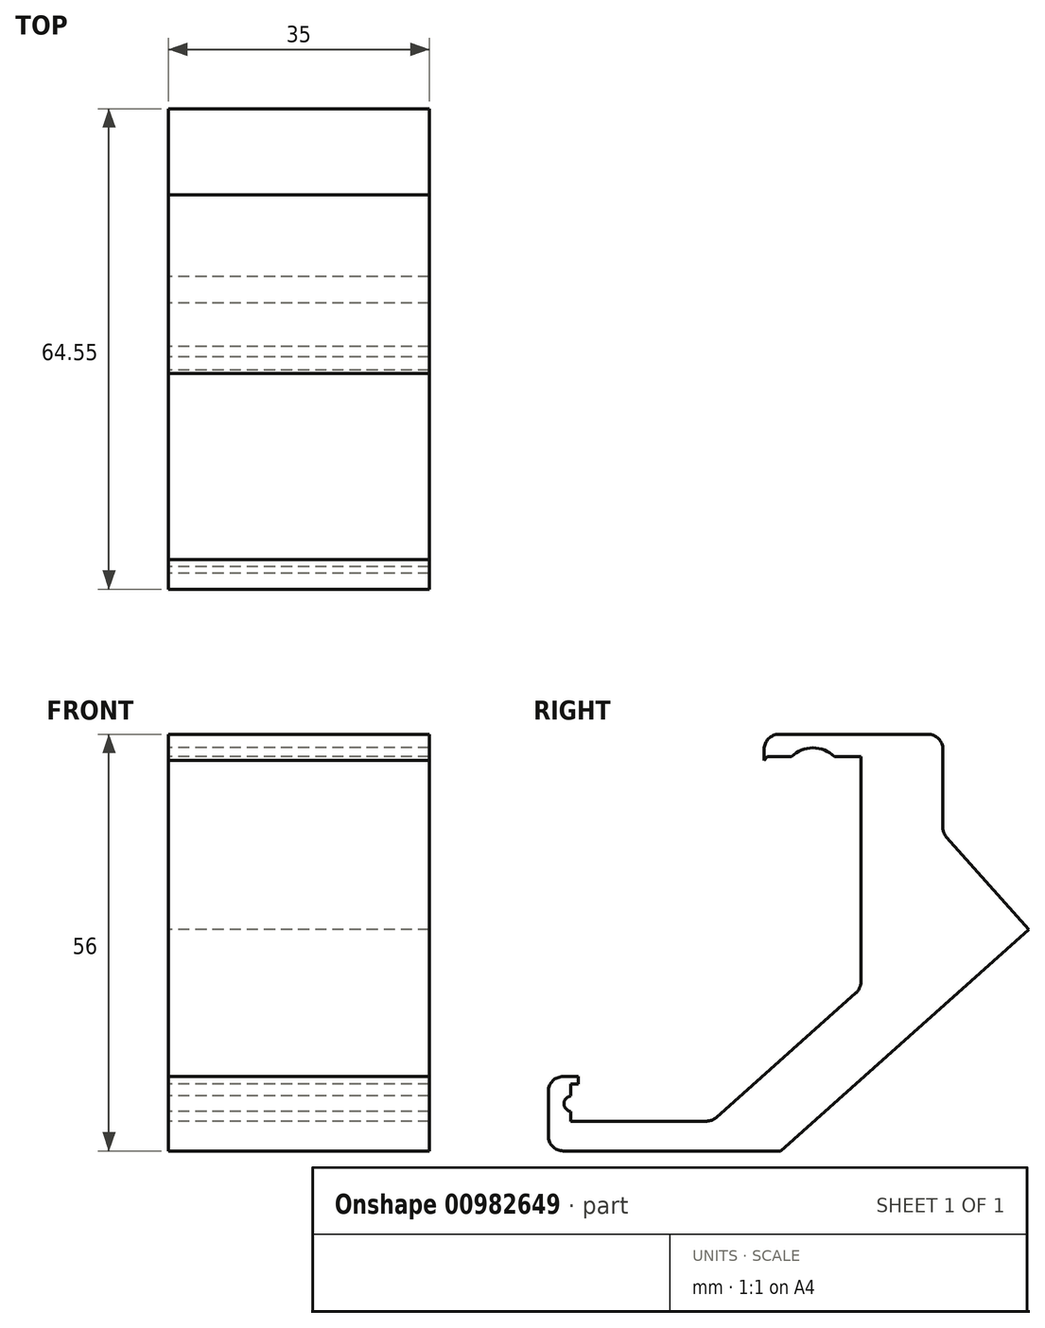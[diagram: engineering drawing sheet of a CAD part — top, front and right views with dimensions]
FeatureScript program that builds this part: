
annotation { "Feature Type Name" : "Feature", "Feature Type Description" : "" }
export const myFeature = defineFeature(function(context is Context, id is Id, definition is map)
    precondition{}
    {
        {
            var Q0;
            Q0=qCreatedBy(makeId("Right.planeOp"),FACE);
            var sketch = newSketch(context, id + "F0", { "sketchPlane" : qUnion([Q0])});
            skLineSegment(sketch, "E0", {"start": v(0, 0) * mm, "end": v(19, 0) * mm});
            skLineSegment(sketch, "E1", {"start": v(19, 0) * mm, "end": v(39, 0) * mm});
            skLineSegment(sketch, "E2", {"start": v(39, 0) * mm, "end": v(39, 49) * mm});
            skLineSegment(sketch, "E3", {"start": v(39, 49) * mm, "end": v(26, 49) * mm});
            skLineSegment(sketch, "E4", {"start": v(0, 0) * mm, "end": v(0, 5) * mm});
            skLineSegment(sketch, "E5", {"start": v(0, 5) * mm, "end": v(1, 5) * mm});
            skLineSegment(sketch, "E6", {"start": v(1, 5) * mm, "end": v(1, 6) * mm});
            skLineSegment(sketch, "E7", {"start": v(1, 6) * mm, "end": v(-3, 6) * mm});
            skLineSegment(sketch, "E8", {"start": v(-3, 6) * mm, "end": v(-3, -4) * mm});
            skLineSegment(sketch, "E9", {"start": v(-3, -4) * mm, "end": v(50, -4) * mm});
            skLineSegment(sketch, "E10", {"start": v(50, -4) * mm, "end": v(50, 52) * mm});
            skLineSegment(sketch, "E11", {"start": v(50, 52) * mm, "end": v(26, 52) * mm});
            skLineSegment(sketch, "E12", {"start": v(26, 52) * mm, "end": v(26, 49) * mm});
            skLineSegment(sketch, "E13", {"start": v(39, 17.85) * mm, "end": v(19, 0) * mm});
            skLineSegment(sketch, "E14", {"start": v(50, 15.46) * mm, "end": v(28.2, -4) * mm});
            skLineSegment(sketch, "E15", {"start": v(50, 15.46) * mm, "end": v(61.55, 25.77) * mm});
            skLineSegment(sketch, "E16", {"start": v(61.55, 25.77) * mm, "end": v(50, 38.72) * mm});
            skSolve(sketch);
        }
        {
            var Q0;
            {var subQ1=sQuery(id+"F0.wireOp",EDGE,"E0");Q0=makeQuery(id+"F0.imprint","IMPRINT",FACE,{"disambiguationData":[TD([[makeQuery(id+"F0.imprint","IMPRINT",EDGE,{"derivedFrom":subQ1}),-1.0]])]});}
            var Q1;
            {var subQ0=sQuery(id+"F0.wireOp",EDGE,"E13");Q1=makeQuery(id+"F0.imprint","IMPRINT",FACE,{"disambiguationData":[TD([[makeQuery(id+"F0.imprint","IMPRINT",EDGE,{"derivedFrom":subQ0}),1.0]])]});}
            var Q2;
            {var subQ0=sQuery(id+"F0.wireOp",EDGE,"E3");Q2=makeQuery(id+"F0.imprint","IMPRINT",FACE,{"disambiguationData":[TD([[makeQuery(id+"F0.imprint","IMPRINT",EDGE,{"derivedFrom":subQ0}),-1.0]])]});}
            var Q3;
            {var subQ0=sQuery(id+"F0.wireOp",EDGE,"E15");Q3=makeQuery(id+"F0.imprint","IMPRINT",FACE,{"disambiguationData":[TD([[makeQuery(id+"F0.imprint","IMPRINT",EDGE,{"derivedFrom":subQ0}),1.0]])]});}
            extrude(context, id + "F1", {"entities" : qUnion([Q0, Q1, Q2, Q3]), "depth" : 35 * mm, "offsetDistance" : 25 * mm});
        }
        {
            var Q0;
            {var subQ0=sQuery(id+"F0.wireOp",EDGE,"E3");Q0=makeQuery(id+"F0.imprint","IMPRINT",FACE,{"disambiguationData":[TD([[makeQuery(id+"F0.imprint","IMPRINT",EDGE,{"derivedFrom":subQ0}),-1.0]])]});}
            var sketch = newSketch(context, id + "F2", { "sketchPlane" : qUnion([Q0])});
            skLineSegment(sketch, "E17", {"start": v(26, 49) * mm, "end": v(26, 48.52) * mm});
            skLineSegment(sketch, "E18", {"start": v(26, 48.52) * mm, "end": v(26.46, 49) * mm});
            skLineSegment(sketch, "E19", {"start": v(26.46, 49) * mm, "end": v(26, 49) * mm});
            skSolve(sketch);
        }
        {
            var Q0;
            Q0=makeQuery(id+"F2.imprint","IMPRINT",FACE,{"disambiguationData":[TD([[makeQuery(id+"F2.imprint","IMPRINT",EDGE,{"derivedFrom":sQuery(id+"F2.wireOp",EDGE,"E17")}),1.0]])]});
            extrude(context, id + "F3", {"entities" : qUnion([Q0]), "operationType" : NewBodyOperationType.ADD, "depth" : 35 * mm, "offsetDistance" : 25 * mm});
        }
        {
            var Q0;
            Q0=qCreatedBy(makeId("Right.planeOp"),FACE);
            var sketch = newSketch(context, id + "F4", { "sketchPlane" : qUnion([Q0])});
            skArc(sketch, "E20", {"start": v(35.45, 49) * mm, "mid": v(32.55, 50.18) * mm, "end": v(29.64, 49) * mm});
            skLineSegment(sketch, "E21", {"start": v(35.45, 49) * mm, "end": v(29.64, 49) * mm});
            skSolve(sketch);
        }
        {
            var Q0;
            Q0 = qSketchRegion(id + "F4", true);
            extrude(context, id + "F5", {"entities" : qUnion([Q0]), "operationType" : NewBodyOperationType.REMOVE, "endBound" : BoundingType.UP_TO_NEXT, "depth" : 58.3 * mm, "offsetDistance" : 25 * mm});
        }
        {
            var Q0;
            {var subQ1=sQuery(id+"F0.wireOp",EDGE,"E0");Q0=makeQuery(id+"F0.imprint","IMPRINT",FACE,{"disambiguationData":[TD([[makeQuery(id+"F0.imprint","IMPRINT",EDGE,{"derivedFrom":subQ1}),-1.0]])]});}
            var sketch = newSketch(context, id + "F6", { "sketchPlane" : qUnion([Q0])});
            skArc(sketch, "E22", {"start": v(0, 3.4) * mm, "mid": v(-0.88, 2.35) * mm, "end": v(0, 1.3) * mm});
            skLineSegment(sketch, "E23", {"start": v(0, 3.4) * mm, "end": v(0, 1.3) * mm});
            skSolve(sketch);
        }
        {
            var Q0;
            Q0=makeQuery(id+"F6.imprint","IMPRINT",FACE,{"disambiguationData":[TD([[makeQuery(id+"F6.imprint","IMPRINT",EDGE,{"derivedFrom":sQuery(id+"F6.wireOp",EDGE,"E22")}),1.0]])]});
            extrude(context, id + "F7", {"entities" : qUnion([Q0]), "operationType" : NewBodyOperationType.REMOVE, "endBound" : BoundingType.THROUGH_ALL, "depth" : 41.48 * mm, "offsetDistance" : 25 * mm});
        }
        {
            var Q0;
            Q0=makeQuery(id+"F1.opExtrude","SWEPT_EDGE",EDGE,{"disambiguationData":[OSD([sQuery(id+"F0.wireOp",EDGE,"E10"),sQuery(id+"F0.wireOp",EDGE,"E11")])]});
            var Q1;
            Q1=makeQuery(id+"F1.opExtrude","SWEPT_EDGE",EDGE,{"disambiguationData":[OSD([sQuery(id+"F0.wireOp",EDGE,"E8"),sQuery(id+"F0.wireOp",EDGE,"E9")])]});
            var Q2;
            Q2=makeQuery(id+"F1.opExtrude","SWEPT_EDGE",EDGE,{"disambiguationData":[OSD([sQuery(id+"F0.wireOp",EDGE,"E7"),sQuery(id+"F0.wireOp",EDGE,"E8")])]});
            var Q3;
            Q3=makeQuery(id+"F1.opExtrude","SWEPT_EDGE",EDGE,{"disambiguationData":[OSD([sQuery(id+"F0.wireOp",EDGE,"E11"),sQuery(id+"F0.wireOp",EDGE,"E12")])]});
            var Q4;
            Q4=makeQuery(id+"F1.opExtrude","SWEPT_EDGE",EDGE,{"disambiguationData":[OSD([sQuery(id+"F0.wireOp",EDGE,"E2"),sQuery(id+"F0.wireOp",EDGE,"E13")])]});
            var Q5;
            Q5=makeQuery(id+"F1.opExtrude","SWEPT_EDGE",EDGE,{"disambiguationData":[OSD([sQuery(id+"F0.wireOp",EDGE,"E0"),sQuery(id+"F0.wireOp",EDGE,"E1"),sQuery(id+"F0.wireOp",EDGE,"E13")])]});
            var Q6;
            Q6=makeQuery(id+"F1.opExtrude","SWEPT_EDGE",EDGE,{"disambiguationData":[OSD([sQuery(id+"F0.wireOp",EDGE,"E10"),sQuery(id+"F0.wireOp",EDGE,"E16")])]});
            fillet(context, id + "F8", {"entities" : qUnion([Q0, Q1, Q2, Q3, Q4, Q5, Q6]), "radius" : 2 * mm, "tangentPropagation" : true, "allowEdgeOverflow" : false});
        }
    });
